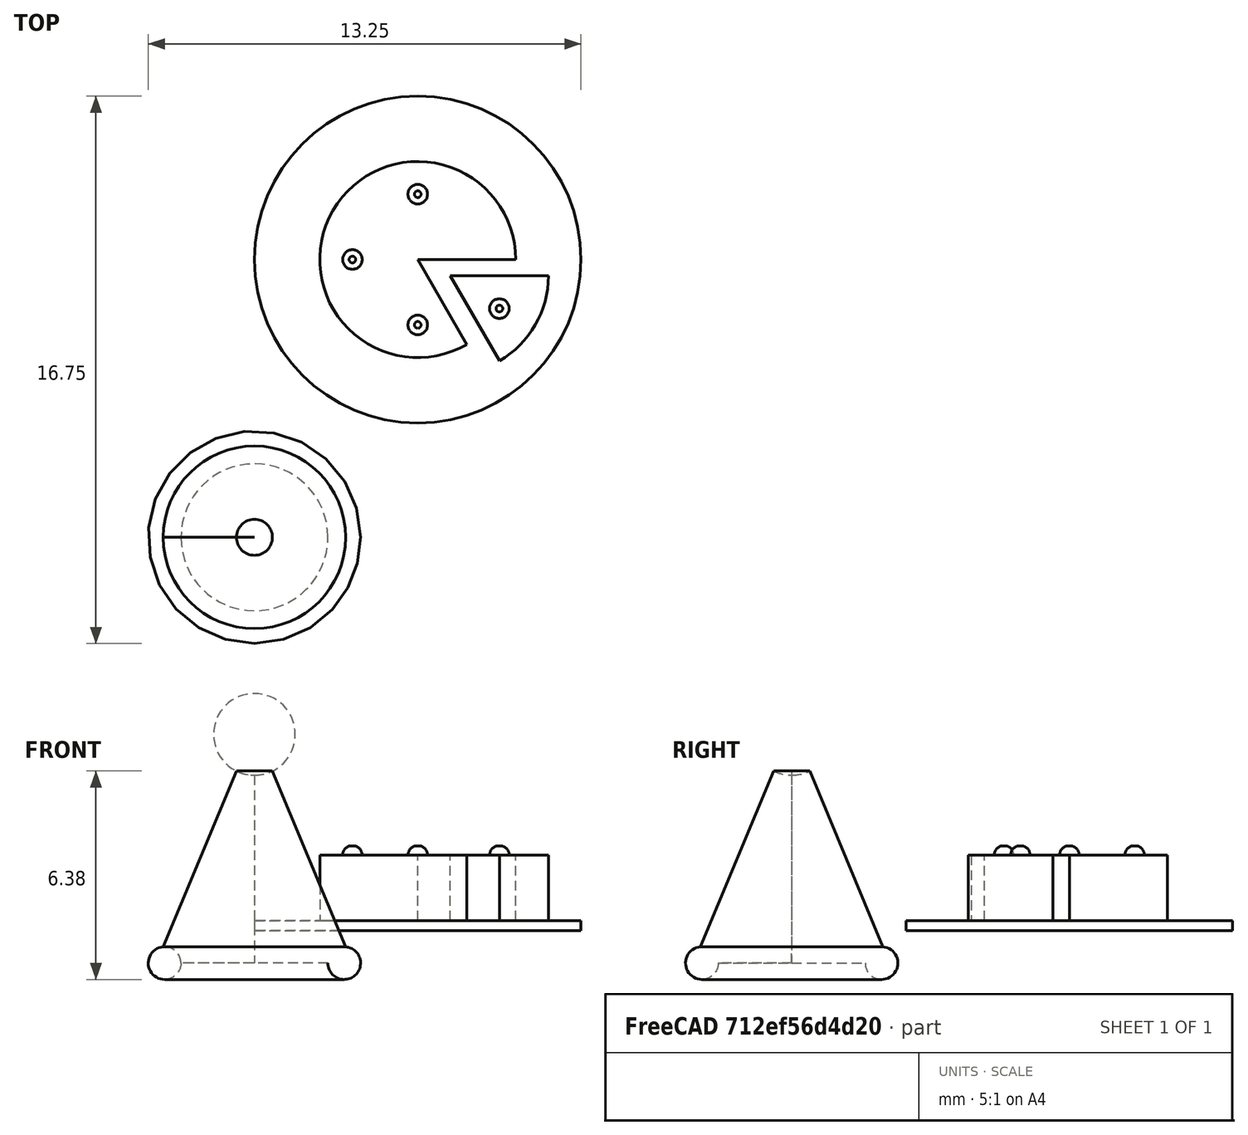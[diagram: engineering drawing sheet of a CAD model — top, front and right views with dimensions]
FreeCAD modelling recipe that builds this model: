
FCSTD DOCUMENT  (FreeCAD 1.0R38806 (Git))
Label: Tarta y sombrero 
License: All rights reserved
LicenseURL: http://en.wikipedia.org/wiki/All_rights_reserved
objects: Part::Sphere×5, Part::Cylinder×3, Part::Scale×2, Part::Cone×1, Part::Torus×1, Part::MultiFuse×1
note: 13 computed .brp shape members not serialized (recipe doc carries the construction recipe); baked Part::Feature solids carry a one-line shape summary decoded from their .brp

FEATURE [Part::Cylinder] Cylinder  label="Tarta"
  Angle = 300
  AttacherType = Attacher::AttachEngine3D
  FirstAngle = 0
  Height = 2
  Placement = pos=(0,0,0.3) rot=(0,0,1;0rad)
  Radius = 3
  SecondAngle = 0
FEATURE [Part::Cylinder] Cylinder001  label="Trozo"
  Angle = 60
  AttacherType = Attacher::AttachEngine3D
  FirstAngle = 0
  Height = 2
  Placement = pos=(1,-0.5,0.3) rot=(0,0,1;-1.0472rad)
  Radius = 3
  SecondAngle = 0
FEATURE [Part::Cylinder] Cylinder002  label="Bandeja"
  Angle = 360
  AttacherType = Attacher::AttachEngine3D
  FirstAngle = 0
  Height = 0.3
  Radius = 5
  SecondAngle = 0
FEATURE [Part::Sphere] Sphere  label="Esfera"
  Angle1 = 0
  Angle2 = 70
  Angle3 = 360
  AttacherType = Attacher::AttachEngine3D
  Placement = pos=(2.5,-1.5,2.3) rot=(0,0,1;0rad)
  Radius = 0.3
FEATURE [Part::Sphere] Sphere001  label="Esfera001"
  Angle1 = 0
  Angle2 = 70
  Angle3 = 360
  AttacherType = Attacher::AttachEngine3D
  Placement = pos=(-2,0,2.3) rot=(0,0,1;0rad)
  Radius = 0.3
FEATURE [Part::Sphere] Sphere002  label="Esfera002"
  Angle1 = 0
  Angle2 = 70
  Angle3 = 360
  AttacherType = Attacher::AttachEngine3D
  Placement = pos=(0,2,2.3) rot=(0,0,1;0rad)
  Radius = 0.3
FEATURE [Part::Sphere] Sphere003  label="Esfera003"
  Angle1 = 0
  Angle2 = 70
  Angle3 = 360
  AttacherType = Attacher::AttachEngine3D
  Placement = pos=(0,-2,2.3) rot=(0,0,1;0rad)
  Radius = 0.3
FEATURE [Part::Cone] Cone  label="Cono"
  Angle = 360
  AttacherType = Attacher::AttachEngine3D
  Height = 12
  Placement = pos=(0,0,10) rot=(0,1,0;3.14159rad)
  Radius1 = 1
  Radius2 = 6
FEATURE [Part::Sphere] Sphere004  label="Esfera004"
  Angle1 = -90
  Angle2 = 90
  Angle3 = 360
  AttacherType = Attacher::AttachEngine3D
  Placement = pos=(0,0,12) rot=(0,0,1;0rad)
  Radius = 2.5
FEATURE [Part::Torus] Torus  label="Toro"
  Angle1 = 180
  Angle2 = -180
  Angle3 = 360
  AttacherType = Attacher::AttachEngine3D
  Placement = pos=(0,0,-2) rot=(0,0,1;0rad)
  Radius1 = 5.5
  Radius2 = 1
FEATURE [Part::MultiFuse] Fusion
  Placement = pos=(10,17,0) rot=(0,0,1;0rad)
  Refine = true
  Shapes = -> [Cone,Sphere004,Torus]
FEATURE [Part::Scale] Scale
  Base = -> Fusion
  Uniform = true
  UniformScale = 0.5
  XScale = 1
  YScale = 1
  ZScale = 1
FEATURE [Part::Scale] Scale001
  Base = -> Fusion
  Uniform = true
  UniformScale = 0.5
  XScale = 1
  YScale = 1
  ZScale = 1
